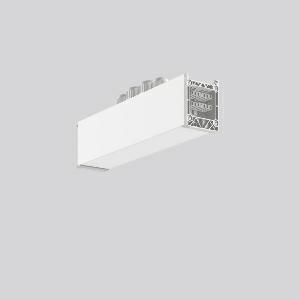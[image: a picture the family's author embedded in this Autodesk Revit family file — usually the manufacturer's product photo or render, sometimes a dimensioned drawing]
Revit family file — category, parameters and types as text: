
# Revit family: linedo_mitteleinspeisung_14pol_b_b_982698_002_1_c4a3
name_source: partatom
category: Lighting Fixtures
units: mm (PartAtom-declared; Revit-internal decimal feet)

## family parameters
Cut with Voids When Loaded = No
Host = Face
Light Source = No
Part Type = Normal
Room Calculation Point = No
Round Connector Dimension = Use Diameter
Shared = No

## types (1)
- LINEDO_Mitteleinspeisung_14pol_B_B
    Apparent Load = 0 VA
    Default Elevation = 1800 mm
    Description = Series: LINEDO
Middle power feed, 14-pole, connection socket / socket. Housing: extruded aluminium profile, powder-coated. Cover made of plastic, surface like housing. LINEDO plug system, plastic, light grey. 4 cable glands (2 x M20 and 2 x M25). Cable glands on top. Easy connection for rigid or flexible wires.
Colour: white
Length: 312 mm
Width: 58 mm
Height: 76 mm
Weight: 850 g
    Height = 76 mm
    Lamp = 0 x
    Length = 312 mm
    Luminous efficacy = 0 lm/W
    Manufacturer = RZB
    ModVariant = No
    Model = 982698.002.1
    Mounting Place = Ceiling
    Mounting Type = Surface mounted, Pendant
    Number of Poles = 1
    OnlyDefault = Yes
    Power Factor = 1
    Product Name = LINEDO_Mitteleinspeisung_14pol_B_B
    Product group = Surface mounted continuous line luminaire system
    ProductGroupID = 310
    Protection Class = Protection class I
    Protection Degree = IP 54
    RLX_Detail_Level = 1
    RLX_Emergency_Light_Flux = 0 lm
    RLX_Emergency_Type = 0
    RLX_Emergency_Type_DB = No
    RlxData = <blob elided: 20825 chars, md5=3d023b19>
    Standby Power = 0 W
    System Light Flux = 0 lm
    System Power = 0 W
    Type Comments = Product without accessories
    Type Image = 982698.002.1.jpg
    URL = http://relux.com
    VarID = ---
    Voltage = 0 V
    Weight = 0.00 kg
    Width = 58 mm

## geometry (parser evidence)
native form markers: Blend x4, Sweep x11
no freeform markers — native parametric forms only
